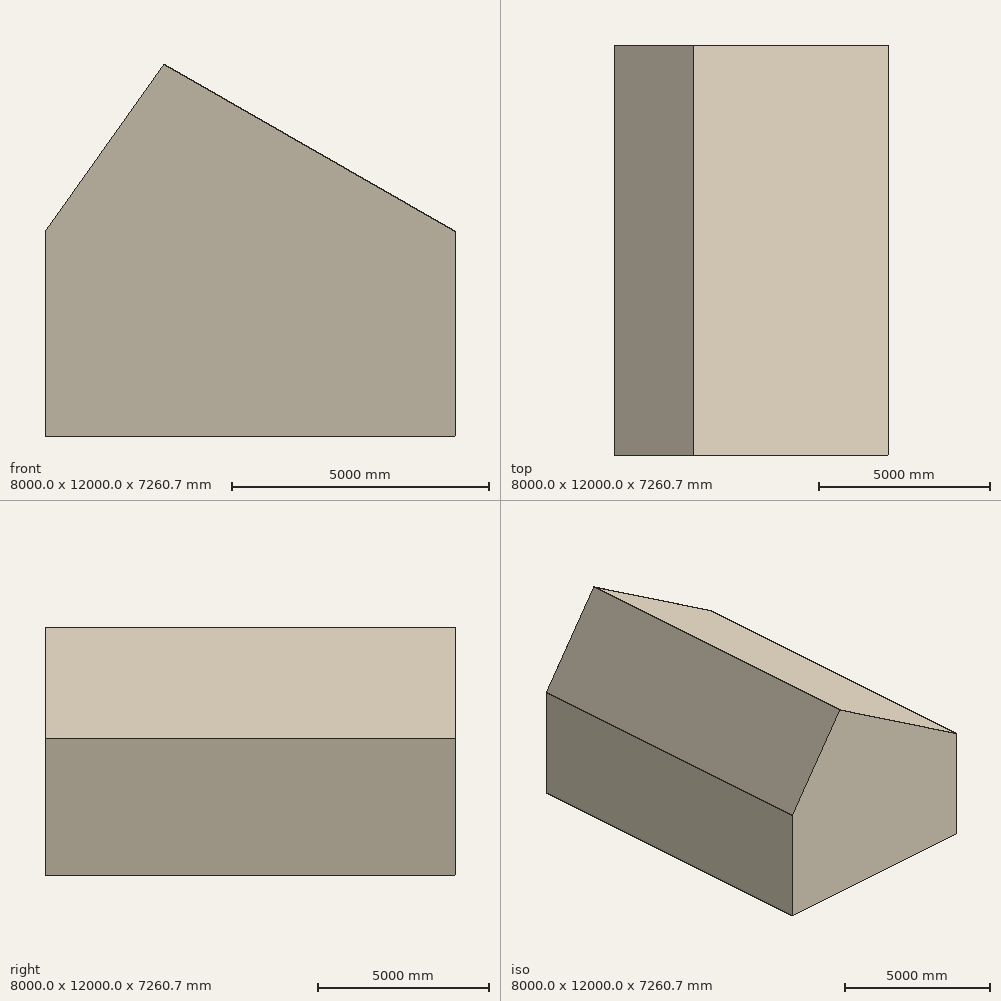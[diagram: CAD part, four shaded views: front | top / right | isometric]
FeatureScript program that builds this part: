
annotation { "Feature Type Name" : "Feature", "Feature Type Description" : "" }
export const myFeature = defineFeature(function(context is Context, id is Id, definition is map)
    precondition{}
    {
        {
            var Q0;
            Q0=qCreatedBy(makeId("Front.planeOp"),FACE);
            var sketch = newSketch(context, id + "F0", { "sketchPlane" : qUnion([Q0])});
            skLineSegment(sketch, "E0", {"start": v(-8000, -4000) * mm, "end": v(-8000, 0) * mm});
            skLineSegment(sketch, "E1", {"start": v(-8000, 0) * mm, "end": v(-5683.17, 3260.72) * mm});
            skLineSegment(sketch, "E2", {"start": v(-5683.17, 3260.72) * mm, "end": v(0, 0) * mm});
            skLineSegment(sketch, "E3", {"start": v(0, 0) * mm, "end": v(0, -4000) * mm});
            skLineSegment(sketch, "E4", {"start": v(0, -4000) * mm, "end": v(-8000, -4000) * mm});
            skSolve(sketch);
        }
        {
            var Q0;
            Q0=makeQuery(id+"F0.imprint","IMPRINT",FACE,{"disambiguationData":[TD([[makeQuery(id+"F0.imprint","IMPRINT",EDGE,{"derivedFrom":sQuery(id+"F0.wireOp",EDGE,"E0")}),-1.0]])]});
            extrude(context, id + "F1", {"entities" : qUnion([Q0]), "depth" : 12000 * mm});
        }
    });
